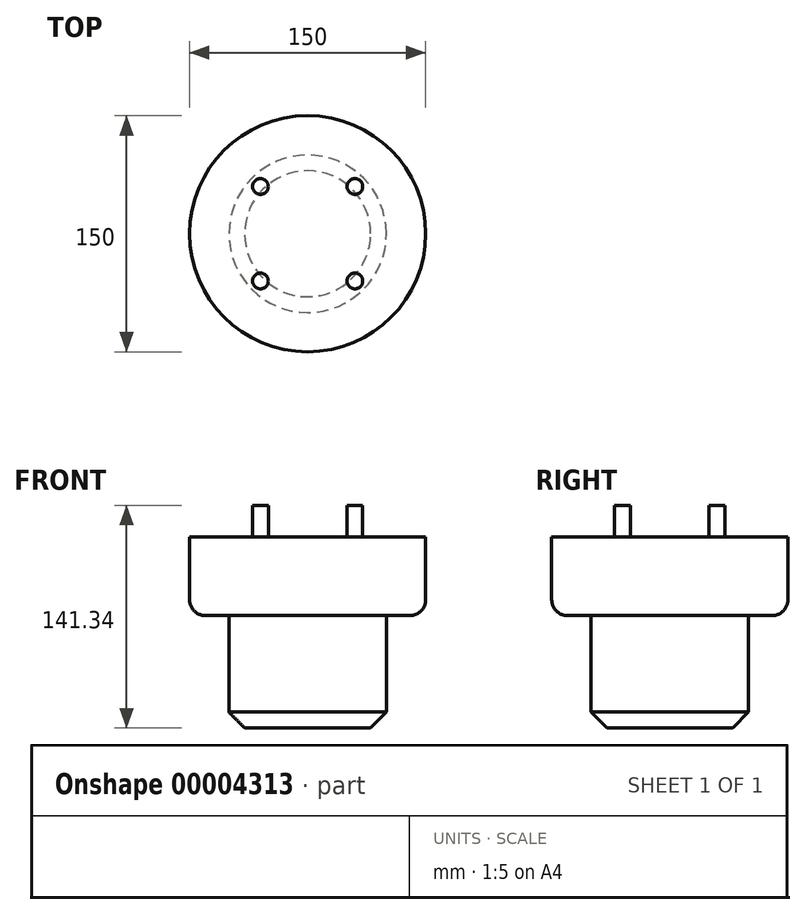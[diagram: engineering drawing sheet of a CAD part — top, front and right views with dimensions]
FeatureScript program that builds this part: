
annotation { "Feature Type Name" : "Feature", "Feature Type Description" : "" }
export const myFeature = defineFeature(function(context is Context, id is Id, definition is map)
    precondition{}
    {
        {
            var Q0;
            Q0=qCreatedBy(makeId("Top.planeOp"),FACE);
            var sketch = newSketch(context, id + "F0", { "sketchPlane" : qUnion([Q0])});
            skLineSegment(sketch, "E0", {"start": v(0, 0) * mm, "end": v(-30, 0) * mm, "construction": true});
            skLineSegment(sketch, "E1", {"start": v(0, 0) * mm, "end": v(30, 0) * mm, "construction": true});
            skLineSegment(sketch, "E2", {"start": v(0, 0) * mm, "end": v(0, -30) * mm, "construction": true});
            skLineSegment(sketch, "E3", {"start": v(0, 0) * mm, "end": v(0, 30) * mm, "construction": true});
            skLineSegment(sketch, "E4.0", {"start": v(0, 30) * mm, "end": v(-30, 30) * mm, "construction": true});
            skLineSegment(sketch, "E4.1", {"start": v(0, 30) * mm, "end": v(30, 30) * mm, "construction": true});
            skLineSegment(sketch, "E5.0", {"start": v(0, -30) * mm, "end": v(-30, -30) * mm, "construction": true});
            skLineSegment(sketch, "E5.1", {"start": v(0, -30) * mm, "end": v(30, -30) * mm, "construction": true});
            skLineSegment(sketch, "E6.0", {"start": v(-30, 0) * mm, "end": v(-30, -30) * mm, "construction": true});
            skLineSegment(sketch, "E6.1", {"start": v(-30, 0) * mm, "end": v(-30, 30) * mm, "construction": true});
            skLineSegment(sketch, "E7.0", {"start": v(30, 0) * mm, "end": v(30, -30) * mm, "construction": true});
            skLineSegment(sketch, "E7.1", {"start": v(30, 0) * mm, "end": v(30, 30) * mm, "construction": true});
            skCircle(sketch, "E8", {"center": v(-30, -30) * mm, "radius": 5 * mm});
            skCircle(sketch, "E9", {"center": v(30, -30) * mm, "radius": 5 * mm});
            skCircle(sketch, "E10", {"center": v(30, 30) * mm, "radius": 5 * mm});
            skCircle(sketch, "E11", {"center": v(-30, 30) * mm, "radius": 5 * mm});
            skSolve(sketch);
        }
        {
            var Q0;
            Q0=qCreatedBy(makeId("Top.planeOp"),FACE);
            var sketch = newSketch(context, id + "F1", { "sketchPlane" : qUnion([Q0])});
            skCircle(sketch, "E12", {"center": v(0, 0) * mm, "radius": 75 * mm});
            skSolve(sketch);
        }
        {
            var Q0;
            Q0=makeQuery(id+"F1.imprint","IMPRINT",FACE,{"disambiguationData":[TD([[makeQuery(id+"F1.imprint","IMPRINT",EDGE,{"derivedFrom":sQuery(id+"F1.wireOp",EDGE,"E12")}),1.0]])]});
            extrude(context, id + "F2", {"entities" : qUnion([Q0]), "oppositeDirection" : true, "depth" : 50 * mm});
        }
        {
            var Q0;
            Q0=makeQuery(id+"F0.imprint","IMPRINT",FACE,{"disambiguationData":[TD([[makeQuery(id+"F0.imprint","IMPRINT",EDGE,{"derivedFrom":sQuery(id+"F0.wireOp",EDGE,"E8")}),1.0]])]});
            var Q1;
            Q1=makeQuery(id+"F0.imprint","IMPRINT",FACE,{"disambiguationData":[TD([[makeQuery(id+"F0.imprint","IMPRINT",EDGE,{"derivedFrom":sQuery(id+"F0.wireOp",EDGE,"E9")}),1.0]])]});
            var Q2;
            Q2=makeQuery(id+"F0.imprint","IMPRINT",FACE,{"disambiguationData":[TD([[makeQuery(id+"F0.imprint","IMPRINT",EDGE,{"derivedFrom":sQuery(id+"F0.wireOp",EDGE,"E10")}),1.0]])]});
            var Q3;
            Q3=makeQuery(id+"F0.imprint","IMPRINT",FACE,{"disambiguationData":[TD([[makeQuery(id+"F0.imprint","IMPRINT",EDGE,{"derivedFrom":sQuery(id+"F0.wireOp",EDGE,"E11")}),1.0]])]});
            extrude(context, id + "F3", {"entities" : qUnion([Q0, Q1, Q2, Q3]), "operationType" : NewBodyOperationType.ADD, "depth" : 20 * mm});
        }
        {
            var Q0;
            Q0=makeQuery(id+"F2.opExtrude","CAP_FACE",FACE,{"disambiguationData":[OSD([sQuery(id+"F1.wireOp",EDGE,"E12")])],"isStart":false});
            var sketch = newSketch(context, id + "F4", { "sketchPlane" : qUnion([Q0])});
            skCircle(sketch, "E13", {"center": v(0, 0) * mm, "radius": 50 * mm});
            skSolve(sketch);
        }
        {
            var Q0;
            Q0=makeQuery(id+"F4.imprint","IMPRINT",FACE,{"disambiguationData":[TD([[makeQuery(id+"F4.imprint","IMPRINT",EDGE,{"derivedFrom":sQuery(id+"F4.wireOp",EDGE,"E13")}),1.0]])]});
            extrude(context, id + "F5", {"entities" : qUnion([Q0]), "operationType" : NewBodyOperationType.ADD, "depth" : 71.34 * mm});
        }
        {
            var Q0;
            Q0=makeQuery(id+"F2.opExtrude","CAP_EDGE",EDGE,{"disambiguationData":[OSD([sQuery(id+"F1.wireOp",EDGE,"E12")])],"isStart":false});
            fillet(context, id + "F6", {"entities" : qUnion([Q0]), "radius" : 10 * mm, "tangentPropagation" : true, "allowEdgeOverflow" : false});
        }
        {
            var Q0;
            Q0=makeQuery(id+"F5.opExtrude","CAP_FACE",FACE,{"disambiguationData":[OSD([sQuery(id+"F4.wireOp",EDGE,"E13")])],"isStart":false});
            chamfer(context, id + "F7", {"entities" : qUnion([Q0]), "width" : 10 * mm, "tangentPropagation" : true});
        }
    });
